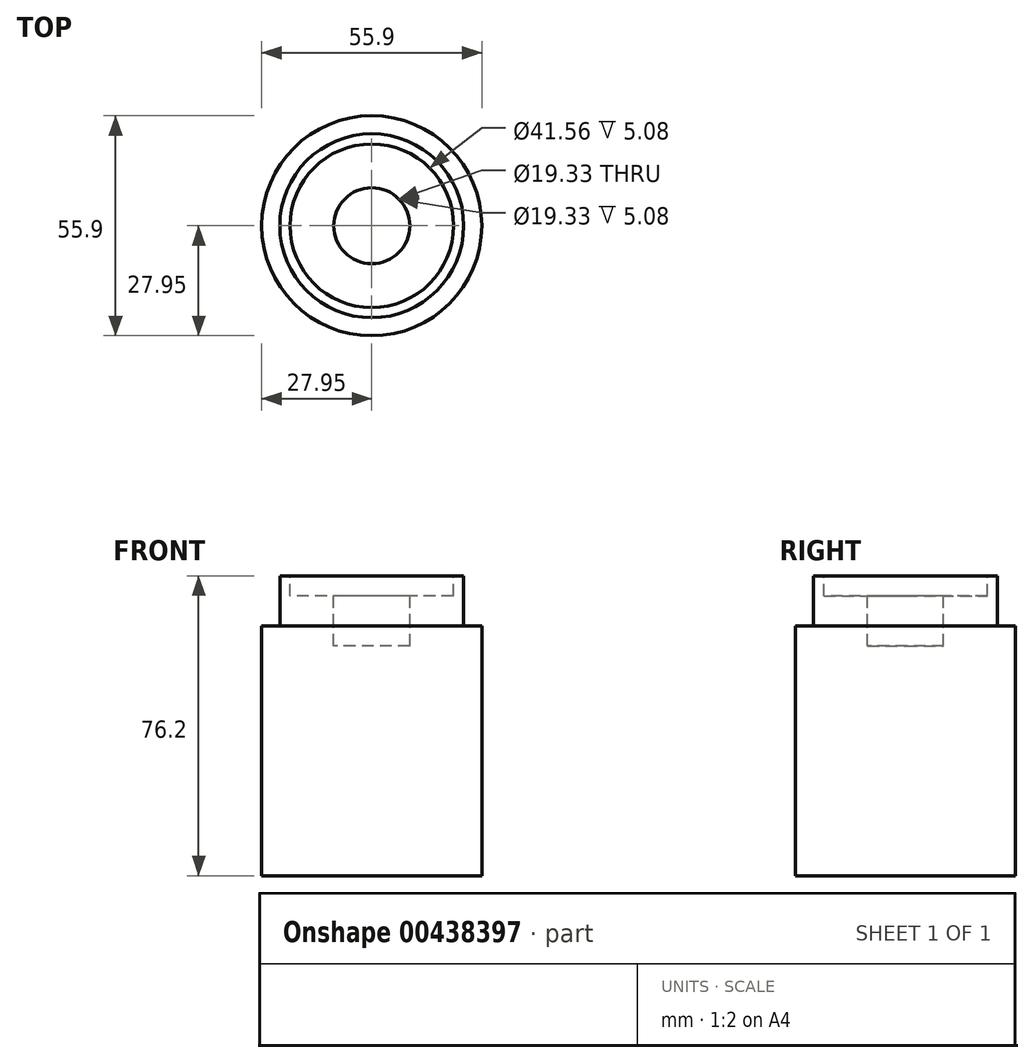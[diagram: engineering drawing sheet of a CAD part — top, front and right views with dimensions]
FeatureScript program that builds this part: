
annotation { "Feature Type Name" : "Feature", "Feature Type Description" : "" }
export const myFeature = defineFeature(function(context is Context, id is Id, definition is map)
    precondition{}
    {
        {
            var Q0;
            Q0=qCreatedBy(makeId("Top.planeOp"),FACE);
            var sketch = newSketch(context, id + "F0", { "sketchPlane" : qUnion([Q0])});
            skCircle(sketch, "E0", {"center": v(0, 0) * mm, "radius": 27.95 * mm});
            skSolve(sketch);
        }
        {
            var Q0;
            Q0=makeQuery(id+"F0.imprint","IMPRINT",FACE,{"disambiguationData":[TD([[makeQuery(id+"F0.imprint","IMPRINT",EDGE,{"derivedFrom":sQuery(id+"F0.wireOp",EDGE,"E0")}),1.0]])]});
            var Q1;
            Q1=sQuery(id+"F0.wireOp",EDGE,"E0");
            extrude(context, id + "F1", {"entities" : qUnion([Q0]), "surfaceEntities" : qUnion([Q1]), "depth" : 63.5 * mm});
        }
        {
            var Q0;
            Q0=makeQuery(id+"F1.opExtrude","CAP_FACE",FACE,{"disambiguationData":[OSD([sQuery(id+"F0.wireOp",EDGE,"E0")])],"isStart":false});
            var sketch = newSketch(context, id + "F2", { "sketchPlane" : qUnion([Q0])});
            skCircle(sketch, "E1", {"center": v(0, 0) * mm, "radius": 23.36 * mm});
            skSolve(sketch);
        }
        {
            var Q0;
            Q0=makeQuery(id+"F2.imprint","IMPRINT",FACE,{"disambiguationData":[TD([[makeQuery(id+"F2.imprint","IMPRINT",EDGE,{"derivedFrom":sQuery(id+"F2.wireOp",EDGE,"E1")}),1.0]])]});
            var Q1;
            Q1=sQuery(id+"F2.wireOp",EDGE,"E1");
            extrude(context, id + "F3", {"entities" : qUnion([Q0]), "surfaceEntities" : qUnion([Q1]), "depth" : 12.7 * mm});
        }
        {
            var Q0;
            Q0=makeQuery(id+"F3.opExtrude","CAP_FACE",FACE,{"disambiguationData":[OSD([sQuery(id+"F2.wireOp",EDGE,"E1")])],"isStart":false});
            var sketch = newSketch(context, id + "F4", { "sketchPlane" : qUnion([Q0])});
            skCircle(sketch, "E2", {"center": v(0, 0) * mm, "radius": 20.78 * mm});
            skSolve(sketch);
        }
        {
            var Q0;
            Q0=makeQuery(id+"F4.imprint","IMPRINT",FACE,{"disambiguationData":[TD([[makeQuery(id+"F4.imprint","IMPRINT",EDGE,{"derivedFrom":sQuery(id+"F4.wireOp",EDGE,"E2")}),1.0]])]});
            var Q1;
            Q1=sQuery(id+"F4.wireOp",EDGE,"E2");
            extrude(context, id + "F5", {"entities" : qUnion([Q0]), "operationType" : NewBodyOperationType.REMOVE, "surfaceEntities" : qUnion([Q1]), "depth" : -5.08 * mm});
        }
        {
            var Q0;
            Q0=makeQuery(id+"F5.boolean.opBoolean","COPY",FACE,{"derivedFrom":makeQuery(id+"F5.opExtrude","CAP_FACE",FACE,{"disambiguationData":[OSD([sQuery(id+"F4.wireOp",EDGE,"E2")])],"isStart":false})});
            var sketch = newSketch(context, id + "F6", { "sketchPlane" : qUnion([Q0])});
            skCircle(sketch, "E3", {"center": v(0, 0) * mm, "radius": 9.67 * mm});
            skSolve(sketch);
        }
        {
            var Q0;
            Q0=makeQuery(id+"F6.imprint","IMPRINT",FACE,{"disambiguationData":[TD([[makeQuery(id+"F6.imprint","IMPRINT",EDGE,{"derivedFrom":sQuery(id+"F6.wireOp",EDGE,"E3")}),1.0]])]});
            var Q1;
            Q1=sQuery(id+"F6.wireOp",EDGE,"E3");
            extrude(context, id + "F7", {"entities" : qUnion([Q0]), "operationType" : NewBodyOperationType.REMOVE, "surfaceEntities" : qUnion([Q1]), "oppositeDirection" : true, "depth" : 12.7 * mm});
        }
    });
